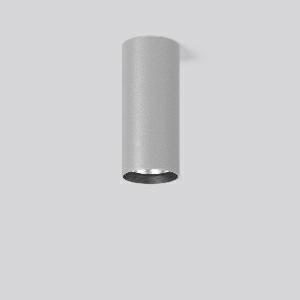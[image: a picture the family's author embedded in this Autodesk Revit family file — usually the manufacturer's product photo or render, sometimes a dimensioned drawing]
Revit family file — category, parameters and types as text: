
# Revit family: heledon_mini_a_931209_004_1_53cb
name_source: partatom
category: Lighting Fixtures
units: mm (PartAtom-declared; Revit-internal decimal feet)

## family parameters
Cut with Voids When Loaded = No
Host = Face
Light Source = No
Part Type = Normal
Room Calculation Point = No
Round Connector Dimension = Use Diameter
Shared = No

## types (1)
- HELEDON mini A (1 x LED Modul 940, 3700 lm, 4000)
    Apparent Load = 29 VA
    Approval mark = CE
    CIE Flux Codes = 99 100 100 100 100
    Color Rendering = 92
    Color Temperature = 4000
    Default Elevation = 1800 mm
    Description = Series: HELEDON mini
Cylindrical surface-mounted downlight. Housing: die-cast aluminium, powder-coated. Internal ceiling frame polycarbonate with bayonet mounting. Black plastic ring and recessed LED to prevent glare from the side. Optical assembly with reflector made of MIRO-Silver with 98% total light reflection for outstanding efficiency - can be changed without tools. Best colour rendering index Ra>90. Suitable for Ceiling mounting. Easy installation with a separate ceiling frame with bayonet mounting and plug connection. Driver integrated. Connected via plug-in connector. High quality converter without flickering and stroboscopic effect. The following accessories can be mounted without use of tools: interchangeable lenses, decorative glasses, honeycomb louvre, clear and frosted diffusers, white interchangeable plastic ring. 
Colour: silver
Diameter: 87 mm
Height: 197 mm
Lamp: LED
Socket: without socket
Colour temperature: 4000K
Colour rendering index (CRI): 92
System power: 29 W
Rated luminous flux: 3700 lm
Luminous efficiency: 128 lm/W
Control gear: Regulated power supply
Protection class: I
Type of protection: IP 20
    Height = 197 mm
    Lamp = 1 x LED Modul 940
    Lamp Light Flux = 3700 lm
    Lamp count = 1
    Length = 87 mm
    Lifetime = 50000 h
    Luminous efficacy = 128 lm/W
    Manufacturer = RZB
    ModVariant = No
    Model = 931209.004.1
    Mounting Place = Ceiling
    Mounting Type = Surface mounted
    Number of Poles = 1
    OnlyDefault = Yes
    Power Factor = 1
    Product Name = HELEDON mini A
    Product group = Surface mounted downlights
    ProductGroupID = 302
    Protection Class = Protection class I
    Protection Degree = IP 20
    RLX_Detail_Level = 1
    RLX_Emergency_Light_Flux = 0 lm
    RLX_Emergency_Type = 0
    RLX_Emergency_Type_DB = No
    RlxData = <blob elided: 106881 chars, md5=c1ee8b8a>
    Socket = socket
    Standby Power = 0 W
    System Light Flux = 3700 lm
    System Power = 29 W
    Type Comments = Product without accessories
    Type Image = 931188.004.jpg
    URL = http://relux.com
    VarID = ---
    Voltage = 230 V
    Voltage Range = 220-240 V
    Weight = 0.00 kg
    Width = 0 mm  [stored 0 ft]

note: [stored X ft] marks values corroborated as IEEE doubles in the binary element streams (Revit-internal decimal feet)

## geometry (parser evidence)
native form markers: Blend x4, Sweep x9
no freeform markers — native parametric forms only
